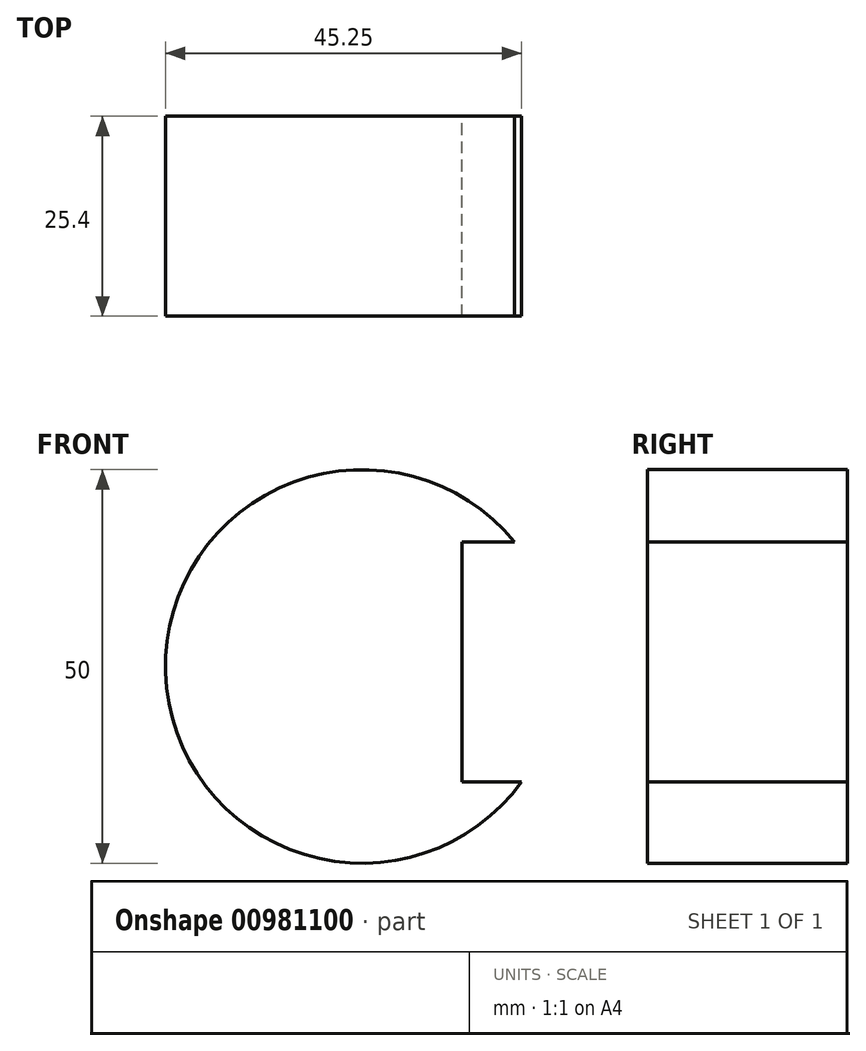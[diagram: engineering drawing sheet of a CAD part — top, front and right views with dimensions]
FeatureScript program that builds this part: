
annotation { "Feature Type Name" : "Feature", "Feature Type Description" : "" }
export const myFeature = defineFeature(function(context is Context, id is Id, definition is map)
    precondition{}
    {
        {
            var Q0;
            Q0=qCreatedBy(makeId("Front.planeOp"),FACE);
            var sketch = newSketch(context, id + "F0", { "sketchPlane" : qUnion([Q0])});
            skCircle(sketch, "E0", {"center": v(0, 0) * mm, "radius": 25 * mm});
            skLineSegment(sketch, "E1.bottom", {"start": v(12.7, 15.82) * mm, "end": v(32.47, 15.82) * mm});
            skLineSegment(sketch, "E1.top", {"start": v(12.7, -14.66) * mm, "end": v(32.47, -14.66) * mm});
            skLineSegment(sketch, "E1.left", {"start": v(12.7, 15.82) * mm, "end": v(12.7, -14.66) * mm});
            skLineSegment(sketch, "E1.right", {"start": v(32.47, 15.82) * mm, "end": v(32.47, -14.66) * mm});
            skSolve(sketch);
        }
        {
            var Q0;
            {var subQ5=sQuery(id+"F0.wireOp",EDGE,"E1.left");Q0=makeQuery(id+"F0.imprint","IMPRINT",FACE,{"disambiguationData":[TD([[makeQuery(id+"F0.imprint","IMPRINT",EDGE,{"derivedFrom":subQ5}),-1.0]])]});}
            extrude(context, id + "F1", {"entities" : qUnion([Q0]), "depth" : 25.4 * mm, "offsetDistance" : 25.4 * mm});
        }
    });
